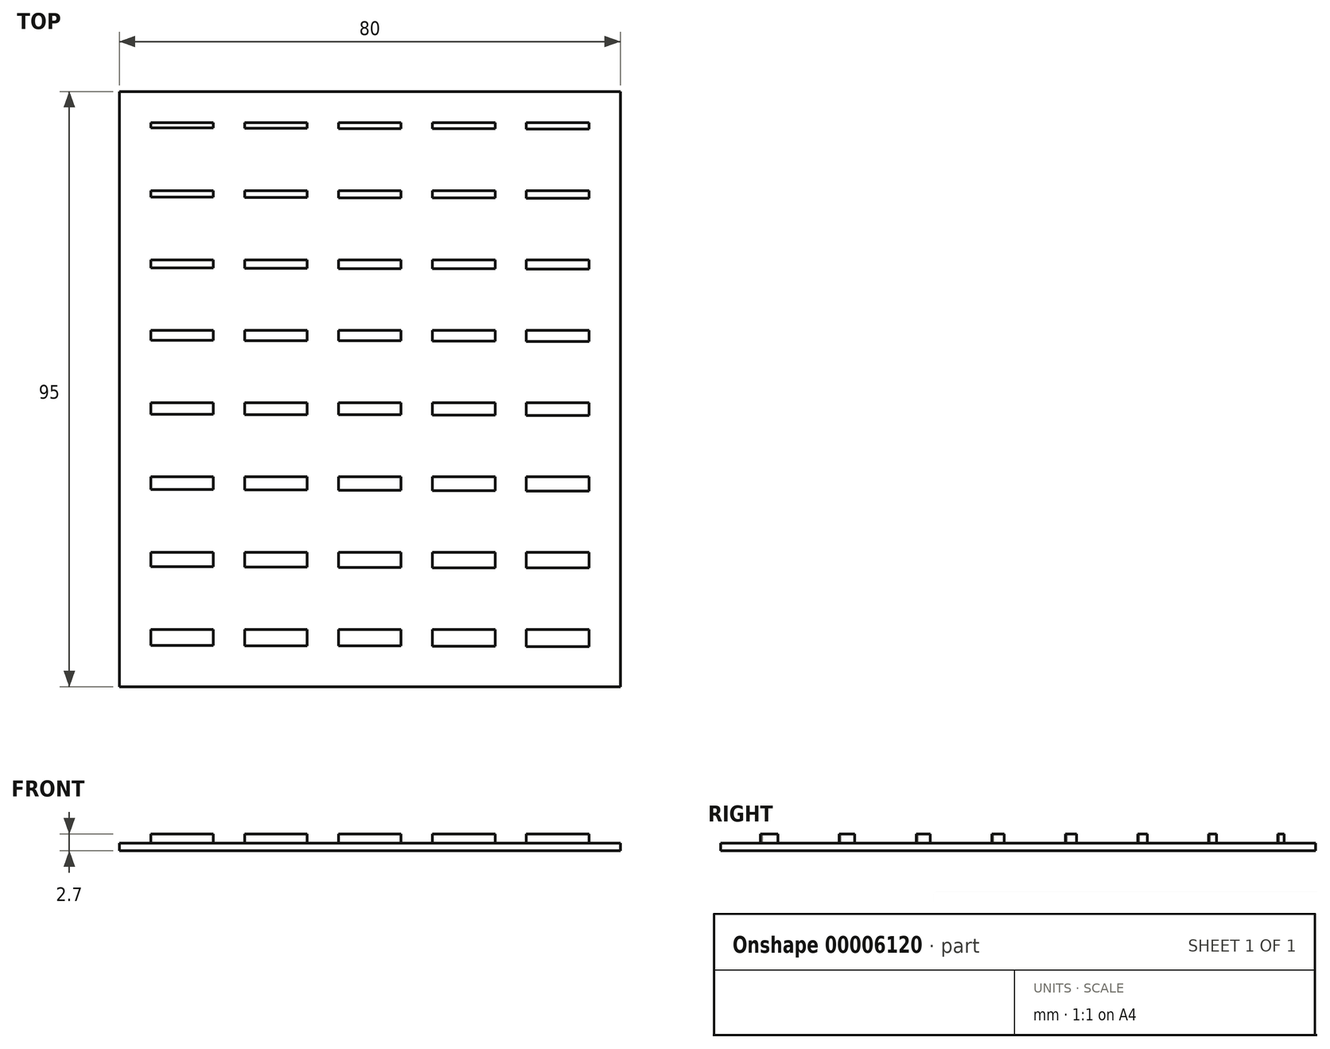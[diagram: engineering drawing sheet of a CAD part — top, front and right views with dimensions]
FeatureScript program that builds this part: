
annotation { "Feature Type Name" : "Feature", "Feature Type Description" : "" }
export const myFeature = defineFeature(function(context is Context, id is Id, definition is map)
    precondition{}
    {
        {
            var Q0;
            Q0=qCreatedBy(makeId("Top.planeOp"),FACE);
            var sketch = newSketch(context, id + "F0", { "sketchPlane" : qUnion([Q0])});
            skLineSegment(sketch, "E0.bottom", {"start": v(-5, 5) * mm, "end": v(75, 5) * mm});
            skLineSegment(sketch, "E0.top", {"start": v(-5, -90) * mm, "end": v(75, -90) * mm});
            skLineSegment(sketch, "E0.left", {"start": v(-5, 5) * mm, "end": v(-5, -90) * mm});
            skLineSegment(sketch, "E0.right", {"start": v(75, 5) * mm, "end": v(75, -90) * mm});
            skSolve(sketch);
        }
        {
            var Q0;
            Q0 = qSketchRegion(id + "F0", true);
            extrude(context, id + "F1", {"entities" : qUnion([Q0]), "depth" : 1.2 * mm});
        }
        {
            var Q0;
            Q0=makeQuery(id+"F1.opExtrude","CAP_FACE",FACE,{"disambiguationData":[OSD([sQuery(id+"F0.wireOp",EDGE,"E0.bottom"),sQuery(id+"F0.wireOp",EDGE,"E0.top"),sQuery(id+"F0.wireOp",EDGE,"E0.left"),sQuery(id+"F0.wireOp",EDGE,"E0.right")])],"isStart":false});
            var sketch = newSketch(context, id + "F2", { "sketchPlane" : qUnion([Q0])});
            skLineSegment(sketch, "E1.bottom", {"start": v(0, 0) * mm, "end": v(10, 0) * mm});
            skLineSegment(sketch, "E1.top", {"start": v(0, -0.8) * mm, "end": v(10, -0.8) * mm});
            skLineSegment(sketch, "E1.left", {"start": v(0, 0) * mm, "end": v(0, -0.8) * mm});
            skLineSegment(sketch, "E1.right", {"start": v(10, 0) * mm, "end": v(10, -0.8) * mm});
            skLineSegment(sketch, "E2.bottom", {"start": v(30, 0) * mm, "end": v(40, 0) * mm});
            skLineSegment(sketch, "E2.top", {"start": v(30, -0.9) * mm, "end": v(40, -0.9) * mm});
            skLineSegment(sketch, "E2.left", {"start": v(30, 0) * mm, "end": v(30, -0.9) * mm});
            skLineSegment(sketch, "E2.right", {"start": v(40, 0) * mm, "end": v(40, -0.9) * mm});
            skLineSegment(sketch, "E3.bottom", {"start": v(15, 0) * mm, "end": v(25, 0) * mm});
            skLineSegment(sketch, "E3.top", {"start": v(15, -0.85) * mm, "end": v(25, -0.85) * mm});
            skLineSegment(sketch, "E3.left", {"start": v(15, 0) * mm, "end": v(15, -0.85) * mm});
            skLineSegment(sketch, "E3.right", {"start": v(25, 0) * mm, "end": v(25, -0.85) * mm});
            skLineSegment(sketch, "E4.bottom", {"start": v(45, 0) * mm, "end": v(55, 0) * mm});
            skLineSegment(sketch, "E4.top", {"start": v(45, -0.95) * mm, "end": v(55, -0.95) * mm});
            skLineSegment(sketch, "E4.left", {"start": v(45, 0) * mm, "end": v(45, -0.95) * mm});
            skLineSegment(sketch, "E4.right", {"start": v(55, 0) * mm, "end": v(55, -0.95) * mm});
            skLineSegment(sketch, "E5.bottom", {"start": v(60, 0) * mm, "end": v(70, 0) * mm});
            skLineSegment(sketch, "E5.top", {"start": v(60, -1) * mm, "end": v(70, -1) * mm});
            skLineSegment(sketch, "E5.left", {"start": v(60, 0) * mm, "end": v(60, -1) * mm});
            skLineSegment(sketch, "E5.right", {"start": v(70, 0) * mm, "end": v(70, -1) * mm});
            skLineSegment(sketch, "E6.top", {"start": v(30, -11.95) * mm, "end": v(40, -11.95) * mm});
            skLineSegment(sketch, "E7.top", {"start": v(0, -11.85) * mm, "end": v(10, -11.85) * mm});
            skLineSegment(sketch, "E8.top", {"start": v(15, -11.9) * mm, "end": v(25, -11.9) * mm});
            skLineSegment(sketch, "E9.top", {"start": v(60, -12.05) * mm, "end": v(70, -12.05) * mm});
            skLineSegment(sketch, "E10.top", {"start": v(45, -12) * mm, "end": v(55, -12) * mm});
            skLineSegment(sketch, "E6.bottom", {"start": v(30, -10.8) * mm, "end": v(40, -10.8) * mm});
            skLineSegment(sketch, "E7.bottom", {"start": v(0, -10.8) * mm, "end": v(10, -10.8) * mm});
            skLineSegment(sketch, "E6.right", {"start": v(40, -10.8) * mm, "end": v(40, -11.95) * mm});
            skLineSegment(sketch, "E8.bottom", {"start": v(15, -10.8) * mm, "end": v(25, -10.8) * mm});
            skLineSegment(sketch, "E10.right", {"start": v(55, -10.8) * mm, "end": v(55, -12) * mm});
            skLineSegment(sketch, "E9.right", {"start": v(70, -10.8) * mm, "end": v(70, -12.05) * mm});
            skLineSegment(sketch, "E10.bottom", {"start": v(45, -10.8) * mm, "end": v(55, -10.8) * mm});
            skLineSegment(sketch, "E9.left", {"start": v(60, -10.8) * mm, "end": v(60, -12.05) * mm});
            skLineSegment(sketch, "E9.bottom", {"start": v(60, -10.8) * mm, "end": v(70, -10.8) * mm});
            skLineSegment(sketch, "E10.left", {"start": v(45, -10.8) * mm, "end": v(45, -12) * mm});
            skLineSegment(sketch, "E6.left", {"start": v(30, -10.8) * mm, "end": v(30, -11.95) * mm});
            skLineSegment(sketch, "E7.right", {"start": v(10, -10.8) * mm, "end": v(10, -11.85) * mm});
            skLineSegment(sketch, "E7.left", {"start": v(0, -10.8) * mm, "end": v(0, -11.85) * mm});
            skLineSegment(sketch, "E8.right", {"start": v(25, -10.8) * mm, "end": v(25, -11.9) * mm});
            skLineSegment(sketch, "E8.left", {"start": v(15, -10.8) * mm, "end": v(15, -11.9) * mm});
            skLineSegment(sketch, "E11.bottom", {"start": v(60, -21.85) * mm, "end": v(70, -21.85) * mm});
            skLineSegment(sketch, "E12.top", {"start": v(30, -34.8) * mm, "end": v(40, -34.8) * mm});
            skLineSegment(sketch, "E13.top", {"start": v(60, -34.9) * mm, "end": v(70, -34.9) * mm});
            skLineSegment(sketch, "E14.bottom", {"start": v(45, -21.85) * mm, "end": v(55, -21.85) * mm});
            skLineSegment(sketch, "E13.bottom", {"start": v(60, -33.15) * mm, "end": v(70, -33.15) * mm});
            skLineSegment(sketch, "E15.bottom", {"start": v(15, -33.15) * mm, "end": v(25, -33.15) * mm});
            skLineSegment(sketch, "E16.top", {"start": v(45, -34.85) * mm, "end": v(55, -34.85) * mm});
            skLineSegment(sketch, "E17.top", {"start": v(0, -34.7) * mm, "end": v(10, -34.7) * mm});
            skLineSegment(sketch, "E11.top", {"start": v(60, -23.35) * mm, "end": v(70, -23.35) * mm});
            skLineSegment(sketch, "E16.bottom", {"start": v(45, -33.15) * mm, "end": v(55, -33.15) * mm});
            skLineSegment(sketch, "E15.top", {"start": v(15, -34.75) * mm, "end": v(25, -34.75) * mm});
            skLineSegment(sketch, "E12.bottom", {"start": v(30, -33.15) * mm, "end": v(40, -33.15) * mm});
            skLineSegment(sketch, "E18.top", {"start": v(15, -23.2) * mm, "end": v(25, -23.2) * mm});
            skLineSegment(sketch, "E18.bottom", {"start": v(15, -21.85) * mm, "end": v(25, -21.85) * mm});
            skLineSegment(sketch, "E19.top", {"start": v(30, -23.25) * mm, "end": v(40, -23.25) * mm});
            skLineSegment(sketch, "E19.bottom", {"start": v(30, -21.85) * mm, "end": v(40, -21.85) * mm});
            skLineSegment(sketch, "E20.top", {"start": v(0, -23.15) * mm, "end": v(10, -23.15) * mm});
            skLineSegment(sketch, "E20.bottom", {"start": v(0, -21.85) * mm, "end": v(10, -21.85) * mm});
            skLineSegment(sketch, "E14.top", {"start": v(45, -23.3) * mm, "end": v(55, -23.3) * mm});
            skLineSegment(sketch, "E17.bottom", {"start": v(0, -33.15) * mm, "end": v(10, -33.15) * mm});
            skLineSegment(sketch, "E12.right", {"start": v(40, -33.15) * mm, "end": v(40, -34.8) * mm});
            skLineSegment(sketch, "E13.left", {"start": v(60, -33.15) * mm, "end": v(60, -34.9) * mm});
            skLineSegment(sketch, "E16.right", {"start": v(55, -33.15) * mm, "end": v(55, -34.85) * mm});
            skLineSegment(sketch, "E15.left", {"start": v(15, -33.15) * mm, "end": v(15, -34.75) * mm});
            skLineSegment(sketch, "E13.right", {"start": v(70, -33.15) * mm, "end": v(70, -34.9) * mm});
            skLineSegment(sketch, "E15.right", {"start": v(25, -33.15) * mm, "end": v(25, -34.75) * mm});
            skLineSegment(sketch, "E14.right", {"start": v(55, -21.85) * mm, "end": v(55, -23.3) * mm});
            skLineSegment(sketch, "E12.left", {"start": v(30, -33.15) * mm, "end": v(30, -34.8) * mm});
            skLineSegment(sketch, "E11.right", {"start": v(70, -21.85) * mm, "end": v(70, -23.35) * mm});
            skLineSegment(sketch, "E16.left", {"start": v(45, -33.15) * mm, "end": v(45, -34.85) * mm});
            skLineSegment(sketch, "E17.right", {"start": v(10, -33.15) * mm, "end": v(10, -34.7) * mm});
            skLineSegment(sketch, "E18.right", {"start": v(25, -21.85) * mm, "end": v(25, -23.2) * mm});
            skLineSegment(sketch, "E17.left", {"start": v(0, -33.15) * mm, "end": v(0, -34.7) * mm});
            skLineSegment(sketch, "E11.left", {"start": v(60, -21.85) * mm, "end": v(60, -23.35) * mm});
            skLineSegment(sketch, "E18.left", {"start": v(15, -21.85) * mm, "end": v(15, -23.2) * mm});
            skLineSegment(sketch, "E19.right", {"start": v(40, -21.85) * mm, "end": v(40, -23.25) * mm});
            skLineSegment(sketch, "E19.left", {"start": v(30, -21.85) * mm, "end": v(30, -23.25) * mm});
            skLineSegment(sketch, "E20.right", {"start": v(10, -21.85) * mm, "end": v(10, -23.15) * mm});
            skLineSegment(sketch, "E20.left", {"start": v(0, -21.85) * mm, "end": v(0, -23.15) * mm});
            skLineSegment(sketch, "E14.left", {"start": v(45, -21.85) * mm, "end": v(45, -23.3) * mm});
            skLineSegment(sketch, "E21.bottom", {"start": v(45, -80.85) * mm, "end": v(55, -80.85) * mm});
            skLineSegment(sketch, "E22.top", {"start": v(30, -46.6) * mm, "end": v(40, -46.6) * mm});
            skLineSegment(sketch, "E23.bottom", {"start": v(15, -44.7) * mm, "end": v(25, -44.7) * mm});
            skLineSegment(sketch, "E24.bottom", {"start": v(60, -56.5) * mm, "end": v(70, -56.5) * mm});
            skLineSegment(sketch, "E25.bottom", {"start": v(45, -44.7) * mm, "end": v(55, -44.7) * mm});
            skLineSegment(sketch, "E26.bottom", {"start": v(30, -56.5) * mm, "end": v(40, -56.5) * mm});
            skLineSegment(sketch, "E23.top", {"start": v(15, -46.55) * mm, "end": v(25, -46.55) * mm});
            skLineSegment(sketch, "E27.bottom", {"start": v(0, -68.55) * mm, "end": v(10, -68.55) * mm});
            skLineSegment(sketch, "E28.top", {"start": v(30, -83.5) * mm, "end": v(40, -83.5) * mm});
            skLineSegment(sketch, "E29.top", {"start": v(60, -46.7) * mm, "end": v(70, -46.7) * mm});
            skLineSegment(sketch, "E30.top", {"start": v(45, -58.7) * mm, "end": v(55, -58.7) * mm});
            skLineSegment(sketch, "E31.bottom", {"start": v(60, -68.55) * mm, "end": v(70, -68.55) * mm});
            skLineSegment(sketch, "E27.top", {"start": v(0, -70.85) * mm, "end": v(10, -70.85) * mm});
            skLineSegment(sketch, "E31.top", {"start": v(60, -71.05) * mm, "end": v(70, -71.05) * mm});
            skLineSegment(sketch, "E22.bottom", {"start": v(30, -44.7) * mm, "end": v(40, -44.7) * mm});
            skLineSegment(sketch, "E29.bottom", {"start": v(60, -44.7) * mm, "end": v(70, -44.7) * mm});
            skLineSegment(sketch, "E24.top", {"start": v(60, -58.75) * mm, "end": v(70, -58.75) * mm});
            skLineSegment(sketch, "E32.bottom", {"start": v(30, -68.55) * mm, "end": v(40, -68.55) * mm});
            skLineSegment(sketch, "E33.top", {"start": v(0, -46.5) * mm, "end": v(10, -46.5) * mm});
            skLineSegment(sketch, "E33.bottom", {"start": v(0, -44.7) * mm, "end": v(10, -44.7) * mm});
            skLineSegment(sketch, "E25.top", {"start": v(45, -46.65) * mm, "end": v(55, -46.65) * mm});
            skLineSegment(sketch, "E30.bottom", {"start": v(45, -56.5) * mm, "end": v(55, -56.5) * mm});
            skLineSegment(sketch, "E34.top", {"start": v(15, -83.45) * mm, "end": v(25, -83.45) * mm});
            skLineSegment(sketch, "E32.top", {"start": v(30, -70.95) * mm, "end": v(40, -70.95) * mm});
            skLineSegment(sketch, "E35.top", {"start": v(0, -83.4) * mm, "end": v(10, -83.4) * mm});
            skLineSegment(sketch, "E36.top", {"start": v(15, -58.6) * mm, "end": v(25, -58.6) * mm});
            skLineSegment(sketch, "E37.bottom", {"start": v(15, -68.55) * mm, "end": v(25, -68.55) * mm});
            skLineSegment(sketch, "E21.top", {"start": v(45, -83.55) * mm, "end": v(55, -83.55) * mm});
            skLineSegment(sketch, "E38.top", {"start": v(0, -58.55) * mm, "end": v(10, -58.55) * mm});
            skLineSegment(sketch, "E36.bottom", {"start": v(15, -56.5) * mm, "end": v(25, -56.5) * mm});
            skLineSegment(sketch, "E39.bottom", {"start": v(60, -80.85) * mm, "end": v(70, -80.85) * mm});
            skLineSegment(sketch, "E37.top", {"start": v(15, -70.9) * mm, "end": v(25, -70.9) * mm});
            skLineSegment(sketch, "E34.bottom", {"start": v(15, -80.85) * mm, "end": v(25, -80.85) * mm});
            skLineSegment(sketch, "E26.top", {"start": v(30, -58.65) * mm, "end": v(40, -58.65) * mm});
            skLineSegment(sketch, "E40.bottom", {"start": v(45, -68.55) * mm, "end": v(55, -68.55) * mm});
            skLineSegment(sketch, "E35.bottom", {"start": v(0, -80.85) * mm, "end": v(10, -80.85) * mm});
            skLineSegment(sketch, "E28.bottom", {"start": v(30, -80.85) * mm, "end": v(40, -80.85) * mm});
            skLineSegment(sketch, "E38.bottom", {"start": v(0, -56.5) * mm, "end": v(10, -56.5) * mm});
            skLineSegment(sketch, "E39.top", {"start": v(60, -83.6) * mm, "end": v(70, -83.6) * mm});
            skLineSegment(sketch, "E40.top", {"start": v(45, -71) * mm, "end": v(55, -71) * mm});
            skLineSegment(sketch, "E29.left", {"start": v(60, -44.7) * mm, "end": v(60, -46.7) * mm});
            skLineSegment(sketch, "E34.right", {"start": v(25, -80.85) * mm, "end": v(25, -83.45) * mm});
            skLineSegment(sketch, "E31.left", {"start": v(60, -68.55) * mm, "end": v(60, -71.05) * mm});
            skLineSegment(sketch, "E23.right", {"start": v(25, -44.7) * mm, "end": v(25, -46.55) * mm});
            skLineSegment(sketch, "E40.right", {"start": v(55, -68.55) * mm, "end": v(55, -71) * mm});
            skLineSegment(sketch, "E35.left", {"start": v(0, -80.85) * mm, "end": v(0, -83.4) * mm});
            skLineSegment(sketch, "E24.left", {"start": v(60, -56.5) * mm, "end": v(60, -58.75) * mm});
            skLineSegment(sketch, "E39.right", {"start": v(70, -80.85) * mm, "end": v(70, -83.6) * mm});
            skLineSegment(sketch, "E37.right", {"start": v(25, -68.55) * mm, "end": v(25, -70.9) * mm});
            skLineSegment(sketch, "E36.left", {"start": v(15, -56.5) * mm, "end": v(15, -58.6) * mm});
            skLineSegment(sketch, "E25.right", {"start": v(55, -44.7) * mm, "end": v(55, -46.65) * mm});
            skLineSegment(sketch, "E25.left", {"start": v(45, -44.7) * mm, "end": v(45, -46.65) * mm});
            skLineSegment(sketch, "E36.right", {"start": v(25, -56.5) * mm, "end": v(25, -58.6) * mm});
            skLineSegment(sketch, "E30.left", {"start": v(45, -56.5) * mm, "end": v(45, -58.7) * mm});
            skLineSegment(sketch, "E34.left", {"start": v(15, -80.85) * mm, "end": v(15, -83.45) * mm});
            skLineSegment(sketch, "E35.right", {"start": v(10, -80.85) * mm, "end": v(10, -83.4) * mm});
            skLineSegment(sketch, "E40.left", {"start": v(45, -68.55) * mm, "end": v(45, -71) * mm});
            skLineSegment(sketch, "E38.left", {"start": v(0, -56.5) * mm, "end": v(0, -58.55) * mm});
            skLineSegment(sketch, "E24.right", {"start": v(70, -56.5) * mm, "end": v(70, -58.75) * mm});
            skLineSegment(sketch, "E21.left", {"start": v(45, -80.85) * mm, "end": v(45, -83.55) * mm});
            skLineSegment(sketch, "E21.right", {"start": v(55, -80.85) * mm, "end": v(55, -83.55) * mm});
            skLineSegment(sketch, "E27.left", {"start": v(0, -68.55) * mm, "end": v(0, -70.85) * mm});
            skLineSegment(sketch, "E32.left", {"start": v(30, -68.55) * mm, "end": v(30, -70.95) * mm});
            skLineSegment(sketch, "E28.right", {"start": v(40, -80.85) * mm, "end": v(40, -83.5) * mm});
            skLineSegment(sketch, "E30.right", {"start": v(55, -56.5) * mm, "end": v(55, -58.7) * mm});
            skLineSegment(sketch, "E38.right", {"start": v(10, -56.5) * mm, "end": v(10, -58.55) * mm});
            skLineSegment(sketch, "E39.left", {"start": v(60, -80.85) * mm, "end": v(60, -83.6) * mm});
            skLineSegment(sketch, "E31.right", {"start": v(70, -68.55) * mm, "end": v(70, -71.05) * mm});
            skLineSegment(sketch, "E27.right", {"start": v(10, -68.55) * mm, "end": v(10, -70.85) * mm});
            skLineSegment(sketch, "E32.right", {"start": v(40, -68.55) * mm, "end": v(40, -70.95) * mm});
            skLineSegment(sketch, "E26.right", {"start": v(40, -56.5) * mm, "end": v(40, -58.65) * mm});
            skLineSegment(sketch, "E26.left", {"start": v(30, -56.5) * mm, "end": v(30, -58.65) * mm});
            skLineSegment(sketch, "E28.left", {"start": v(30, -80.85) * mm, "end": v(30, -83.5) * mm});
            skLineSegment(sketch, "E29.right", {"start": v(70, -44.7) * mm, "end": v(70, -46.7) * mm});
            skLineSegment(sketch, "E37.left", {"start": v(15, -68.55) * mm, "end": v(15, -70.9) * mm});
            skLineSegment(sketch, "E22.left", {"start": v(30, -44.7) * mm, "end": v(30, -46.6) * mm});
            skLineSegment(sketch, "E22.right", {"start": v(40, -44.7) * mm, "end": v(40, -46.6) * mm});
            skLineSegment(sketch, "E23.left", {"start": v(15, -44.7) * mm, "end": v(15, -46.55) * mm});
            skLineSegment(sketch, "E33.right", {"start": v(10, -44.7) * mm, "end": v(10, -46.5) * mm});
            skLineSegment(sketch, "E33.left", {"start": v(0, -44.7) * mm, "end": v(0, -46.5) * mm});
            skSolve(sketch);
        }
        {
            var Q0;
            Q0 = qSketchRegion(id + "F2", true);
            extrude(context, id + "F3", {"entities" : qUnion([Q0]), "operationType" : NewBodyOperationType.ADD, "depth" : 1.5 * mm});
        }
    });
